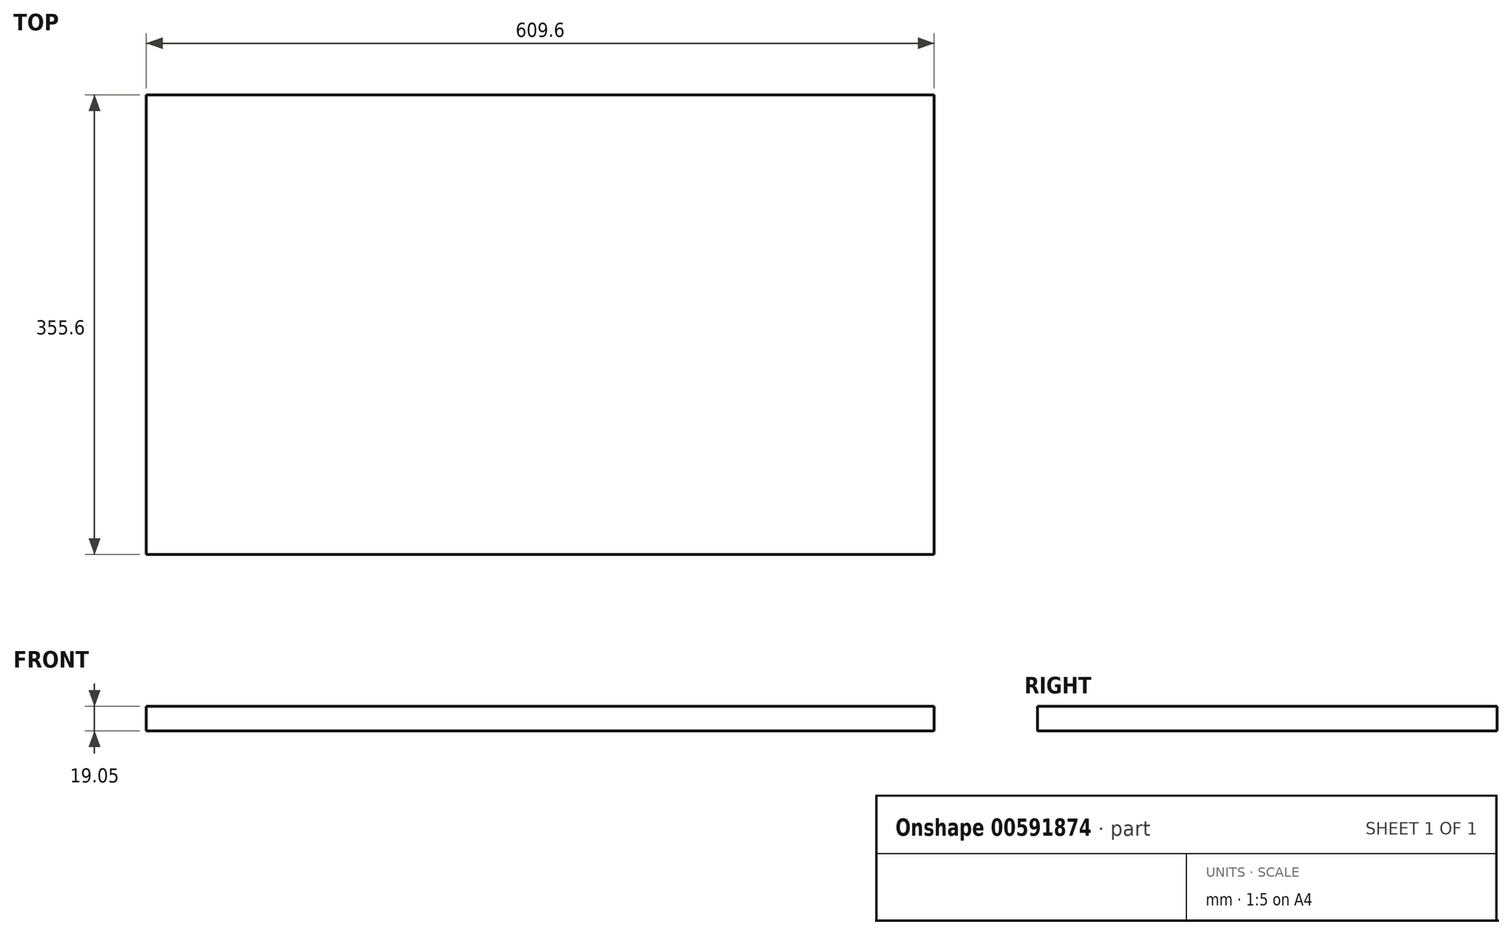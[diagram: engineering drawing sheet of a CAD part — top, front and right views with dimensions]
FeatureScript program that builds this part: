
annotation { "Feature Type Name" : "Feature", "Feature Type Description" : "" }
export const myFeature = defineFeature(function(context is Context, id is Id, definition is map)
    precondition{}
    {
        {
            var Q0;
            Q0=qCreatedBy(makeId("Top.planeOp"),FACE);
            var sketch = newSketch(context, id + "F0", { "sketchPlane" : qUnion([Q0])});
            skLineSegment(sketch, "E0.bottom", {"start": v(304.8, 177.8) * mm, "end": v(-304.8, 177.8) * mm});
            skLineSegment(sketch, "E0.top", {"start": v(304.8, -177.8) * mm, "end": v(-304.8, -177.8) * mm});
            skLineSegment(sketch, "E0.left", {"start": v(304.8, 177.8) * mm, "end": v(304.8, -177.8) * mm});
            skLineSegment(sketch, "E0.right", {"start": v(-304.8, 177.8) * mm, "end": v(-304.8, -177.8) * mm});
            skPoint(sketch, "E0.middle", {"position": v(0, 0) * mm});
            skSolve(sketch);
        }
        {
            var Q0;
            Q0=qSketchRegion(id+"F0",true);
            extrude(context, id + "F1", {"entities" : qUnion([Q0]), "depth" : 19.05 * mm, "offsetDistance" : 25.4 * mm});
        }
    });
